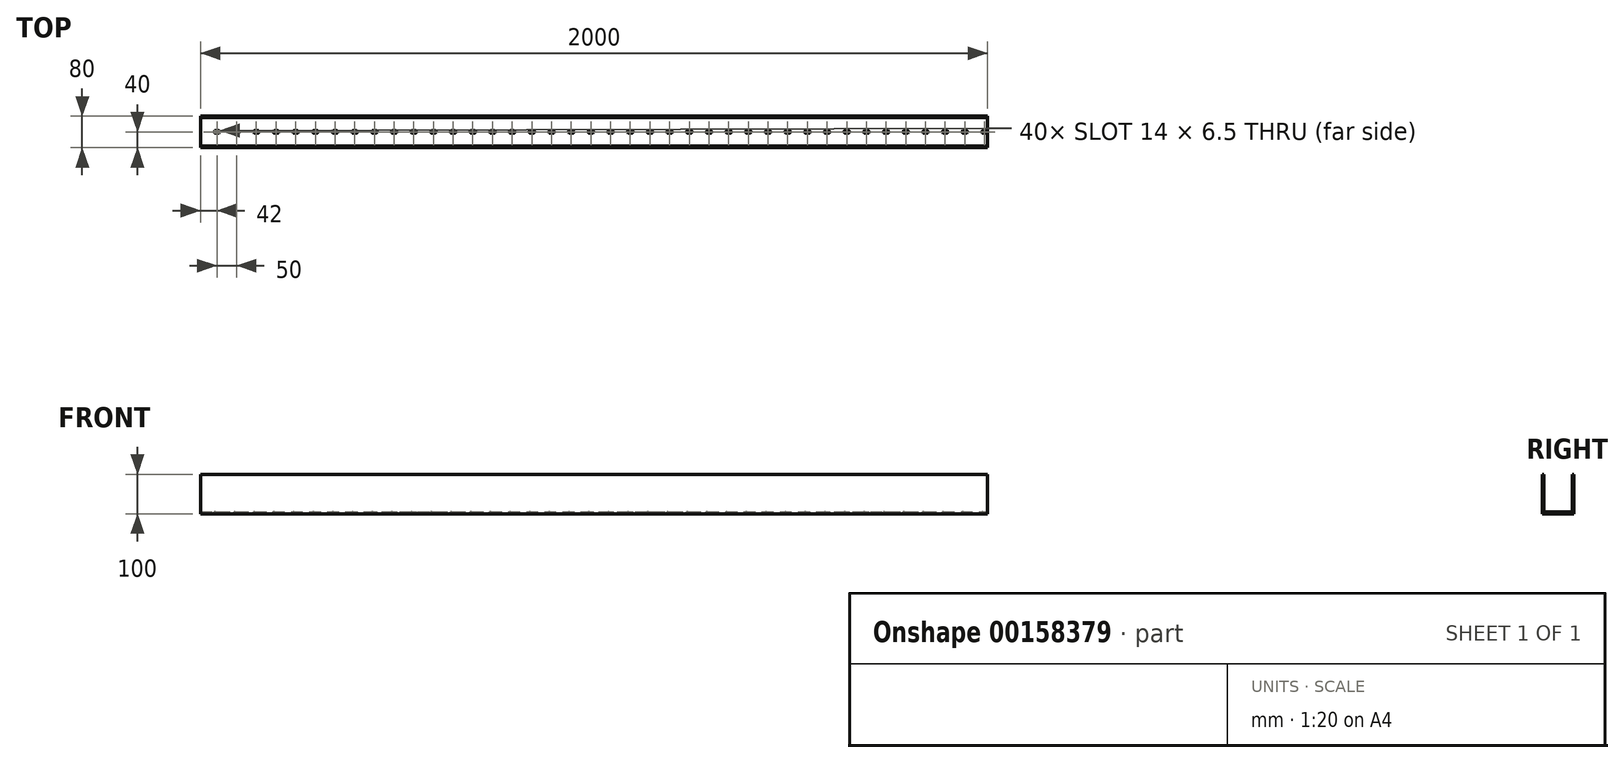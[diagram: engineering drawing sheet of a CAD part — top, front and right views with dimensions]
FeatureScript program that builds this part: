
annotation { "Feature Type Name" : "Feature", "Feature Type Description" : "" }
export const myFeature = defineFeature(function(context is Context, id is Id, definition is map)
    precondition{}
    {
        {
            var Q0;
            Q0=qCreatedBy(makeId("Top.planeOp"),FACE);
            var sketch = newSketch(context, id + "F0", { "sketchPlane" : qUnion([Q0])});
            skLineSegment(sketch, "E0.bottom", {"start": v(0, 0) * mm, "end": v(2000, 0) * mm});
            skLineSegment(sketch, "E0.top", {"start": v(0, 80) * mm, "end": v(2000, 80) * mm});
            skLineSegment(sketch, "E0.left", {"start": v(0, 0) * mm, "end": v(0, 80) * mm});
            skLineSegment(sketch, "E0.right", {"start": v(2000, 0) * mm, "end": v(2000, 80) * mm});
            skSolve(sketch);
        }
        {
            var Q0;
            Q0 = qSketchRegion(id + "F0", true);
            extrude(context, id + "F1", {"entities" : qUnion([Q0]), "depth" : 100 * mm});
        }
        {
            var Q0;
            Q0=makeQuery(id+"F1.opExtrude","CAP_FACE",FACE,{"disambiguationData":[OSD([sQuery(id+"F0.wireOp",EDGE,"E0.bottom"),sQuery(id+"F0.wireOp",EDGE,"E0.top"),sQuery(id+"F0.wireOp",EDGE,"E0.left"),sQuery(id+"F0.wireOp",EDGE,"E0.right")])],"isStart":false});
            var sketch = newSketch(context, id + "F2", { "sketchPlane" : qUnion([Q0])});
            skLineSegment(sketch, "E1.bottom", {"start": v(0, 76) * mm, "end": v(2000, 76) * mm});
            skLineSegment(sketch, "E1.top", {"start": v(0, 4) * mm, "end": v(2000, 4) * mm});
            skLineSegment(sketch, "E1.left", {"start": v(0, 76) * mm, "end": v(0, 4) * mm});
            skLineSegment(sketch, "E1.right", {"start": v(2000, 76) * mm, "end": v(2000, 4) * mm});
            skSolve(sketch);
        }
        {
            var Q0;
            Q0 = qSketchRegion(id + "F2", true);
            extrude(context, id + "F3", {"entities" : qUnion([Q0]), "operationType" : NewBodyOperationType.REMOVE, "oppositeDirection" : true, "depth" : (100 - 4) * mm});
        }
        {
            var Q0;
            Q0=makeQuery(id+"F3.boolean.opBoolean","COPY",FACE,{"derivedFrom":makeQuery(id+"F3.opExtrude","CAP_FACE",FACE,{"disambiguationData":[OSD([sQuery(id+"F2.wireOp",EDGE,"E1.bottom"),sQuery(id+"F2.wireOp",EDGE,"E1.top"),sQuery(id+"F2.wireOp",EDGE,"E1.left"),sQuery(id+"F2.wireOp",EDGE,"E1.right")])],"isStart":false})});
            var sketch = newSketch(context, id + "F4", { "sketchPlane" : qUnion([Q0])});
            skLineSegment(sketch, "E2", {"start": v(38.25, 40) * mm, "end": v(45.75, 40) * mm, "construction": true});
            skArc(sketch, "E3.0.startCap", {"start": v(38.25, 36.75) * mm, "mid": v(35, 40) * mm, "end": v(38.25, 43.25) * mm});
            skArc(sketch, "E3.0.endCap", {"start": v(45.75, 43.25) * mm, "mid": v(49, 40) * mm, "end": v(45.75, 36.75) * mm});
            skLineSegment(sketch, "E3.0.left", {"start": v(38.25, 43.25) * mm, "end": v(45.75, 43.25) * mm});
            skLineSegment(sketch, "E3.0.right", {"start": v(38.25, 36.75) * mm, "end": v(45.75, 36.75) * mm});
            skLineSegment(sketch, "E4.1.0.0", {"start": v(88.25, 36.75) * mm, "end": v(95.75, 36.75) * mm});
            skArc(sketch, "E4.1.0.1", {"start": v(88.25, 36.75) * mm, "mid": v(85, 40) * mm, "end": v(88.25, 43.25) * mm});
            skLineSegment(sketch, "E4.1.0.2", {"start": v(88.25, 43.25) * mm, "end": v(95.75, 43.25) * mm});
            skArc(sketch, "E4.1.0.3", {"start": v(95.75, 43.25) * mm, "mid": v(99, 40) * mm, "end": v(95.75, 36.75) * mm});
            skLineSegment(sketch, "E4.2.0.0", {"start": v(138.25, 36.75) * mm, "end": v(145.75, 36.75) * mm});
            skArc(sketch, "E4.2.0.1", {"start": v(138.25, 36.75) * mm, "mid": v(135, 40) * mm, "end": v(138.25, 43.25) * mm});
            skLineSegment(sketch, "E4.2.0.2", {"start": v(138.25, 43.25) * mm, "end": v(145.75, 43.25) * mm});
            skArc(sketch, "E4.2.0.3", {"start": v(145.75, 43.25) * mm, "mid": v(149, 40) * mm, "end": v(145.75, 36.75) * mm});
            skLineSegment(sketch, "E4.3.0.0", {"start": v(188.25, 36.75) * mm, "end": v(195.75, 36.75) * mm});
            skArc(sketch, "E4.3.0.1", {"start": v(188.25, 36.75) * mm, "mid": v(185, 40) * mm, "end": v(188.25, 43.25) * mm});
            skLineSegment(sketch, "E4.3.0.2", {"start": v(188.25, 43.25) * mm, "end": v(195.75, 43.25) * mm});
            skArc(sketch, "E4.3.0.3", {"start": v(195.75, 43.25) * mm, "mid": v(199, 40) * mm, "end": v(195.75, 36.75) * mm});
            skLineSegment(sketch, "E4.4.0.0", {"start": v(238.25, 36.75) * mm, "end": v(245.75, 36.75) * mm});
            skArc(sketch, "E4.4.0.1", {"start": v(238.25, 36.75) * mm, "mid": v(235, 40) * mm, "end": v(238.25, 43.25) * mm});
            skLineSegment(sketch, "E4.4.0.2", {"start": v(238.25, 43.25) * mm, "end": v(245.75, 43.25) * mm});
            skArc(sketch, "E4.4.0.3", {"start": v(245.75, 43.25) * mm, "mid": v(249, 40) * mm, "end": v(245.75, 36.75) * mm});
            skLineSegment(sketch, "E4.5.0.0", {"start": v(288.25, 36.75) * mm, "end": v(295.75, 36.75) * mm});
            skArc(sketch, "E4.5.0.1", {"start": v(288.25, 36.75) * mm, "mid": v(285, 40) * mm, "end": v(288.25, 43.25) * mm});
            skLineSegment(sketch, "E4.5.0.2", {"start": v(288.25, 43.25) * mm, "end": v(295.75, 43.25) * mm});
            skArc(sketch, "E4.5.0.3", {"start": v(295.75, 43.25) * mm, "mid": v(299, 40) * mm, "end": v(295.75, 36.75) * mm});
            skLineSegment(sketch, "E4.6.0.0", {"start": v(338.25, 36.75) * mm, "end": v(345.75, 36.75) * mm});
            skArc(sketch, "E4.6.0.1", {"start": v(338.25, 36.75) * mm, "mid": v(335, 40) * mm, "end": v(338.25, 43.25) * mm});
            skLineSegment(sketch, "E4.6.0.2", {"start": v(338.25, 43.25) * mm, "end": v(345.75, 43.25) * mm});
            skArc(sketch, "E4.6.0.3", {"start": v(345.75, 43.25) * mm, "mid": v(349, 40) * mm, "end": v(345.75, 36.75) * mm});
            skLineSegment(sketch, "E4.7.0.0", {"start": v(388.25, 36.75) * mm, "end": v(395.75, 36.75) * mm});
            skArc(sketch, "E4.7.0.1", {"start": v(388.25, 36.75) * mm, "mid": v(385, 40) * mm, "end": v(388.25, 43.25) * mm});
            skLineSegment(sketch, "E4.7.0.2", {"start": v(388.25, 43.25) * mm, "end": v(395.75, 43.25) * mm});
            skArc(sketch, "E4.7.0.3", {"start": v(395.75, 43.25) * mm, "mid": v(399, 40) * mm, "end": v(395.75, 36.75) * mm});
            skLineSegment(sketch, "E4.8.0.0", {"start": v(438.25, 36.75) * mm, "end": v(445.75, 36.75) * mm});
            skArc(sketch, "E4.8.0.1", {"start": v(438.25, 36.75) * mm, "mid": v(435, 40) * mm, "end": v(438.25, 43.25) * mm});
            skLineSegment(sketch, "E4.8.0.2", {"start": v(438.25, 43.25) * mm, "end": v(445.75, 43.25) * mm});
            skArc(sketch, "E4.8.0.3", {"start": v(445.75, 43.25) * mm, "mid": v(449, 40) * mm, "end": v(445.75, 36.75) * mm});
            skLineSegment(sketch, "E4.9.0.0", {"start": v(488.25, 36.75) * mm, "end": v(495.75, 36.75) * mm});
            skArc(sketch, "E4.9.0.1", {"start": v(488.25, 36.75) * mm, "mid": v(485, 40) * mm, "end": v(488.25, 43.25) * mm});
            skLineSegment(sketch, "E4.9.0.2", {"start": v(488.25, 43.25) * mm, "end": v(495.75, 43.25) * mm});
            skArc(sketch, "E4.9.0.3", {"start": v(495.75, 43.25) * mm, "mid": v(499, 40) * mm, "end": v(495.75, 36.75) * mm});
            skLineSegment(sketch, "E4.10.0.0", {"start": v(538.25, 36.75) * mm, "end": v(545.75, 36.75) * mm});
            skArc(sketch, "E4.10.0.1", {"start": v(538.25, 36.75) * mm, "mid": v(535, 40) * mm, "end": v(538.25, 43.25) * mm});
            skLineSegment(sketch, "E4.10.0.2", {"start": v(538.25, 43.25) * mm, "end": v(545.75, 43.25) * mm});
            skArc(sketch, "E4.10.0.3", {"start": v(545.75, 43.25) * mm, "mid": v(549, 40) * mm, "end": v(545.75, 36.75) * mm});
            skLineSegment(sketch, "E4.11.0.0", {"start": v(588.25, 36.75) * mm, "end": v(595.75, 36.75) * mm});
            skArc(sketch, "E4.11.0.1", {"start": v(588.25, 36.75) * mm, "mid": v(585, 40) * mm, "end": v(588.25, 43.25) * mm});
            skLineSegment(sketch, "E4.11.0.2", {"start": v(588.25, 43.25) * mm, "end": v(595.75, 43.25) * mm});
            skArc(sketch, "E4.11.0.3", {"start": v(595.75, 43.25) * mm, "mid": v(599, 40) * mm, "end": v(595.75, 36.75) * mm});
            skLineSegment(sketch, "E4.12.0.0", {"start": v(638.25, 36.75) * mm, "end": v(645.75, 36.75) * mm});
            skArc(sketch, "E4.12.0.1", {"start": v(638.25, 36.75) * mm, "mid": v(635, 40) * mm, "end": v(638.25, 43.25) * mm});
            skLineSegment(sketch, "E4.12.0.2", {"start": v(638.25, 43.25) * mm, "end": v(645.75, 43.25) * mm});
            skArc(sketch, "E4.12.0.3", {"start": v(645.75, 43.25) * mm, "mid": v(649, 40) * mm, "end": v(645.75, 36.75) * mm});
            skLineSegment(sketch, "E4.13.0.0", {"start": v(688.25, 36.75) * mm, "end": v(695.75, 36.75) * mm});
            skArc(sketch, "E4.13.0.1", {"start": v(688.25, 36.75) * mm, "mid": v(685, 40) * mm, "end": v(688.25, 43.25) * mm});
            skLineSegment(sketch, "E4.13.0.2", {"start": v(688.25, 43.25) * mm, "end": v(695.75, 43.25) * mm});
            skArc(sketch, "E4.13.0.3", {"start": v(695.75, 43.25) * mm, "mid": v(699, 40) * mm, "end": v(695.75, 36.75) * mm});
            skLineSegment(sketch, "E4.14.0.0", {"start": v(738.25, 36.75) * mm, "end": v(745.75, 36.75) * mm});
            skArc(sketch, "E4.14.0.1", {"start": v(738.25, 36.75) * mm, "mid": v(735, 40) * mm, "end": v(738.25, 43.25) * mm});
            skLineSegment(sketch, "E4.14.0.2", {"start": v(738.25, 43.25) * mm, "end": v(745.75, 43.25) * mm});
            skArc(sketch, "E4.14.0.3", {"start": v(745.75, 43.25) * mm, "mid": v(749, 40) * mm, "end": v(745.75, 36.75) * mm});
            skLineSegment(sketch, "E4.15.0.0", {"start": v(788.25, 36.75) * mm, "end": v(795.75, 36.75) * mm});
            skArc(sketch, "E4.15.0.1", {"start": v(788.25, 36.75) * mm, "mid": v(785, 40) * mm, "end": v(788.25, 43.25) * mm});
            skLineSegment(sketch, "E4.15.0.2", {"start": v(788.25, 43.25) * mm, "end": v(795.75, 43.25) * mm});
            skArc(sketch, "E4.15.0.3", {"start": v(795.75, 43.25) * mm, "mid": v(799, 40) * mm, "end": v(795.75, 36.75) * mm});
            skLineSegment(sketch, "E4.16.0.0", {"start": v(838.25, 36.75) * mm, "end": v(845.75, 36.75) * mm});
            skArc(sketch, "E4.16.0.1", {"start": v(838.25, 36.75) * mm, "mid": v(835, 40) * mm, "end": v(838.25, 43.25) * mm});
            skLineSegment(sketch, "E4.16.0.2", {"start": v(838.25, 43.25) * mm, "end": v(845.75, 43.25) * mm});
            skArc(sketch, "E4.16.0.3", {"start": v(845.75, 43.25) * mm, "mid": v(849, 40) * mm, "end": v(845.75, 36.75) * mm});
            skLineSegment(sketch, "E4.17.0.0", {"start": v(888.25, 36.75) * mm, "end": v(895.75, 36.75) * mm});
            skArc(sketch, "E4.17.0.1", {"start": v(888.25, 36.75) * mm, "mid": v(885, 40) * mm, "end": v(888.25, 43.25) * mm});
            skLineSegment(sketch, "E4.17.0.2", {"start": v(888.25, 43.25) * mm, "end": v(895.75, 43.25) * mm});
            skArc(sketch, "E4.17.0.3", {"start": v(895.75, 43.25) * mm, "mid": v(899, 40) * mm, "end": v(895.75, 36.75) * mm});
            skLineSegment(sketch, "E4.18.0.0", {"start": v(938.25, 36.75) * mm, "end": v(945.75, 36.75) * mm});
            skArc(sketch, "E4.18.0.1", {"start": v(938.25, 36.75) * mm, "mid": v(935, 40) * mm, "end": v(938.25, 43.25) * mm});
            skLineSegment(sketch, "E4.18.0.2", {"start": v(938.25, 43.25) * mm, "end": v(945.75, 43.25) * mm});
            skArc(sketch, "E4.18.0.3", {"start": v(945.75, 43.25) * mm, "mid": v(949, 40) * mm, "end": v(945.75, 36.75) * mm});
            skLineSegment(sketch, "E4.19.0.0", {"start": v(988.25, 36.75) * mm, "end": v(995.75, 36.75) * mm});
            skArc(sketch, "E4.19.0.1", {"start": v(988.25, 36.75) * mm, "mid": v(985, 40) * mm, "end": v(988.25, 43.25) * mm});
            skLineSegment(sketch, "E4.19.0.2", {"start": v(988.25, 43.25) * mm, "end": v(995.75, 43.25) * mm});
            skArc(sketch, "E4.19.0.3", {"start": v(995.75, 43.25) * mm, "mid": v(999, 40) * mm, "end": v(995.75, 36.75) * mm});
            skLineSegment(sketch, "E4.20.0.0", {"start": v(1038.25, 36.75) * mm, "end": v(1045.75, 36.75) * mm});
            skArc(sketch, "E4.20.0.1", {"start": v(1038.25, 36.75) * mm, "mid": v(1035, 40) * mm, "end": v(1038.25, 43.25) * mm});
            skLineSegment(sketch, "E4.20.0.2", {"start": v(1038.25, 43.25) * mm, "end": v(1045.75, 43.25) * mm});
            skArc(sketch, "E4.20.0.3", {"start": v(1045.75, 43.25) * mm, "mid": v(1049, 40) * mm, "end": v(1045.75, 36.75) * mm});
            skLineSegment(sketch, "E4.21.0.0", {"start": v(1088.25, 36.75) * mm, "end": v(1095.75, 36.75) * mm});
            skArc(sketch, "E4.21.0.1", {"start": v(1088.25, 36.75) * mm, "mid": v(1085, 40) * mm, "end": v(1088.25, 43.25) * mm});
            skLineSegment(sketch, "E4.21.0.2", {"start": v(1088.25, 43.25) * mm, "end": v(1095.75, 43.25) * mm});
            skArc(sketch, "E4.21.0.3", {"start": v(1095.75, 43.25) * mm, "mid": v(1099, 40) * mm, "end": v(1095.75, 36.75) * mm});
            skLineSegment(sketch, "E4.22.0.0", {"start": v(1138.25, 36.75) * mm, "end": v(1145.75, 36.75) * mm});
            skArc(sketch, "E4.22.0.1", {"start": v(1138.25, 36.75) * mm, "mid": v(1135, 40) * mm, "end": v(1138.25, 43.25) * mm});
            skLineSegment(sketch, "E4.22.0.2", {"start": v(1138.25, 43.25) * mm, "end": v(1145.75, 43.25) * mm});
            skArc(sketch, "E4.22.0.3", {"start": v(1145.75, 43.25) * mm, "mid": v(1149, 40) * mm, "end": v(1145.75, 36.75) * mm});
            skLineSegment(sketch, "E4.23.0.0", {"start": v(1188.25, 36.75) * mm, "end": v(1195.75, 36.75) * mm});
            skArc(sketch, "E4.23.0.1", {"start": v(1188.25, 36.75) * mm, "mid": v(1185, 40) * mm, "end": v(1188.25, 43.25) * mm});
            skLineSegment(sketch, "E4.23.0.2", {"start": v(1188.25, 43.25) * mm, "end": v(1195.75, 43.25) * mm});
            skArc(sketch, "E4.23.0.3", {"start": v(1195.75, 43.25) * mm, "mid": v(1199, 40) * mm, "end": v(1195.75, 36.75) * mm});
            skLineSegment(sketch, "E4.24.0.0", {"start": v(1238.25, 36.75) * mm, "end": v(1245.75, 36.75) * mm});
            skArc(sketch, "E4.24.0.1", {"start": v(1238.25, 36.75) * mm, "mid": v(1235, 40) * mm, "end": v(1238.25, 43.25) * mm});
            skLineSegment(sketch, "E4.24.0.2", {"start": v(1238.25, 43.25) * mm, "end": v(1245.75, 43.25) * mm});
            skArc(sketch, "E4.24.0.3", {"start": v(1245.75, 43.25) * mm, "mid": v(1249, 40) * mm, "end": v(1245.75, 36.75) * mm});
            skLineSegment(sketch, "E4.25.0.0", {"start": v(1288.25, 36.75) * mm, "end": v(1295.75, 36.75) * mm});
            skArc(sketch, "E4.25.0.1", {"start": v(1288.25, 36.75) * mm, "mid": v(1285, 40) * mm, "end": v(1288.25, 43.25) * mm});
            skLineSegment(sketch, "E4.25.0.2", {"start": v(1288.25, 43.25) * mm, "end": v(1295.75, 43.25) * mm});
            skArc(sketch, "E4.25.0.3", {"start": v(1295.75, 43.25) * mm, "mid": v(1299, 40) * mm, "end": v(1295.75, 36.75) * mm});
            skLineSegment(sketch, "E4.26.0.0", {"start": v(1338.25, 36.75) * mm, "end": v(1345.75, 36.75) * mm});
            skArc(sketch, "E4.26.0.1", {"start": v(1338.25, 36.75) * mm, "mid": v(1335, 40) * mm, "end": v(1338.25, 43.25) * mm});
            skLineSegment(sketch, "E4.26.0.2", {"start": v(1338.25, 43.25) * mm, "end": v(1345.75, 43.25) * mm});
            skArc(sketch, "E4.26.0.3", {"start": v(1345.75, 43.25) * mm, "mid": v(1349, 40) * mm, "end": v(1345.75, 36.75) * mm});
            skLineSegment(sketch, "E4.27.0.0", {"start": v(1388.25, 36.75) * mm, "end": v(1395.75, 36.75) * mm});
            skArc(sketch, "E4.27.0.1", {"start": v(1388.25, 36.75) * mm, "mid": v(1385, 40) * mm, "end": v(1388.25, 43.25) * mm});
            skLineSegment(sketch, "E4.27.0.2", {"start": v(1388.25, 43.25) * mm, "end": v(1395.75, 43.25) * mm});
            skArc(sketch, "E4.27.0.3", {"start": v(1395.75, 43.25) * mm, "mid": v(1399, 40) * mm, "end": v(1395.75, 36.75) * mm});
            skLineSegment(sketch, "E4.28.0.0", {"start": v(1438.25, 36.75) * mm, "end": v(1445.75, 36.75) * mm});
            skArc(sketch, "E4.28.0.1", {"start": v(1438.25, 36.75) * mm, "mid": v(1435, 40) * mm, "end": v(1438.25, 43.25) * mm});
            skLineSegment(sketch, "E4.28.0.2", {"start": v(1438.25, 43.25) * mm, "end": v(1445.75, 43.25) * mm});
            skArc(sketch, "E4.28.0.3", {"start": v(1445.75, 43.25) * mm, "mid": v(1449, 40) * mm, "end": v(1445.75, 36.75) * mm});
            skLineSegment(sketch, "E4.29.0.0", {"start": v(1488.25, 36.75) * mm, "end": v(1495.75, 36.75) * mm});
            skArc(sketch, "E4.29.0.1", {"start": v(1488.25, 36.75) * mm, "mid": v(1485, 40) * mm, "end": v(1488.25, 43.25) * mm});
            skLineSegment(sketch, "E4.29.0.2", {"start": v(1488.25, 43.25) * mm, "end": v(1495.75, 43.25) * mm});
            skArc(sketch, "E4.29.0.3", {"start": v(1495.75, 43.25) * mm, "mid": v(1499, 40) * mm, "end": v(1495.75, 36.75) * mm});
            skLineSegment(sketch, "E4.30.0.0", {"start": v(1538.25, 36.75) * mm, "end": v(1545.75, 36.75) * mm});
            skArc(sketch, "E4.30.0.1", {"start": v(1538.25, 36.75) * mm, "mid": v(1535, 40) * mm, "end": v(1538.25, 43.25) * mm});
            skLineSegment(sketch, "E4.30.0.2", {"start": v(1538.25, 43.25) * mm, "end": v(1545.75, 43.25) * mm});
            skArc(sketch, "E4.30.0.3", {"start": v(1545.75, 43.25) * mm, "mid": v(1549, 40) * mm, "end": v(1545.75, 36.75) * mm});
            skLineSegment(sketch, "E4.31.0.0", {"start": v(1588.25, 36.75) * mm, "end": v(1595.75, 36.75) * mm});
            skArc(sketch, "E4.31.0.1", {"start": v(1588.25, 36.75) * mm, "mid": v(1585, 40) * mm, "end": v(1588.25, 43.25) * mm});
            skLineSegment(sketch, "E4.31.0.2", {"start": v(1588.25, 43.25) * mm, "end": v(1595.75, 43.25) * mm});
            skArc(sketch, "E4.31.0.3", {"start": v(1595.75, 43.25) * mm, "mid": v(1599, 40) * mm, "end": v(1595.75, 36.75) * mm});
            skLineSegment(sketch, "E4.32.0.0", {"start": v(1638.25, 36.75) * mm, "end": v(1645.75, 36.75) * mm});
            skArc(sketch, "E4.32.0.1", {"start": v(1638.25, 36.75) * mm, "mid": v(1635, 40) * mm, "end": v(1638.25, 43.25) * mm});
            skLineSegment(sketch, "E4.32.0.2", {"start": v(1638.25, 43.25) * mm, "end": v(1645.75, 43.25) * mm});
            skArc(sketch, "E4.32.0.3", {"start": v(1645.75, 43.25) * mm, "mid": v(1649, 40) * mm, "end": v(1645.75, 36.75) * mm});
            skLineSegment(sketch, "E4.33.0.0", {"start": v(1688.25, 36.75) * mm, "end": v(1695.75, 36.75) * mm});
            skArc(sketch, "E4.33.0.1", {"start": v(1688.25, 36.75) * mm, "mid": v(1685, 40) * mm, "end": v(1688.25, 43.25) * mm});
            skLineSegment(sketch, "E4.33.0.2", {"start": v(1688.25, 43.25) * mm, "end": v(1695.75, 43.25) * mm});
            skArc(sketch, "E4.33.0.3", {"start": v(1695.75, 43.25) * mm, "mid": v(1699, 40) * mm, "end": v(1695.75, 36.75) * mm});
            skLineSegment(sketch, "E4.34.0.0", {"start": v(1738.25, 36.75) * mm, "end": v(1745.75, 36.75) * mm});
            skArc(sketch, "E4.34.0.1", {"start": v(1738.25, 36.75) * mm, "mid": v(1735, 40) * mm, "end": v(1738.25, 43.25) * mm});
            skLineSegment(sketch, "E4.34.0.2", {"start": v(1738.25, 43.25) * mm, "end": v(1745.75, 43.25) * mm});
            skArc(sketch, "E4.34.0.3", {"start": v(1745.75, 43.25) * mm, "mid": v(1749, 40) * mm, "end": v(1745.75, 36.75) * mm});
            skLineSegment(sketch, "E4.35.0.0", {"start": v(1788.25, 36.75) * mm, "end": v(1795.75, 36.75) * mm});
            skArc(sketch, "E4.35.0.1", {"start": v(1788.25, 36.75) * mm, "mid": v(1785, 40) * mm, "end": v(1788.25, 43.25) * mm});
            skLineSegment(sketch, "E4.35.0.2", {"start": v(1788.25, 43.25) * mm, "end": v(1795.75, 43.25) * mm});
            skArc(sketch, "E4.35.0.3", {"start": v(1795.75, 43.25) * mm, "mid": v(1799, 40) * mm, "end": v(1795.75, 36.75) * mm});
            skLineSegment(sketch, "E4.36.0.0", {"start": v(1838.25, 36.75) * mm, "end": v(1845.75, 36.75) * mm});
            skArc(sketch, "E4.36.0.1", {"start": v(1838.25, 36.75) * mm, "mid": v(1835, 40) * mm, "end": v(1838.25, 43.25) * mm});
            skLineSegment(sketch, "E4.36.0.2", {"start": v(1838.25, 43.25) * mm, "end": v(1845.75, 43.25) * mm});
            skArc(sketch, "E4.36.0.3", {"start": v(1845.75, 43.25) * mm, "mid": v(1849, 40) * mm, "end": v(1845.75, 36.75) * mm});
            skLineSegment(sketch, "E4.37.0.0", {"start": v(1888.25, 36.75) * mm, "end": v(1895.75, 36.75) * mm});
            skArc(sketch, "E4.37.0.1", {"start": v(1888.25, 36.75) * mm, "mid": v(1885, 40) * mm, "end": v(1888.25, 43.25) * mm});
            skLineSegment(sketch, "E4.37.0.2", {"start": v(1888.25, 43.25) * mm, "end": v(1895.75, 43.25) * mm});
            skArc(sketch, "E4.37.0.3", {"start": v(1895.75, 43.25) * mm, "mid": v(1899, 40) * mm, "end": v(1895.75, 36.75) * mm});
            skLineSegment(sketch, "E4.38.0.0", {"start": v(1938.25, 36.75) * mm, "end": v(1945.75, 36.75) * mm});
            skArc(sketch, "E4.38.0.1", {"start": v(1938.25, 36.75) * mm, "mid": v(1935, 40) * mm, "end": v(1938.25, 43.25) * mm});
            skLineSegment(sketch, "E4.38.0.2", {"start": v(1938.25, 43.25) * mm, "end": v(1945.75, 43.25) * mm});
            skArc(sketch, "E4.38.0.3", {"start": v(1945.75, 43.25) * mm, "mid": v(1949, 40) * mm, "end": v(1945.75, 36.75) * mm});
            skLineSegment(sketch, "E4.39.0.0", {"start": v(1988.25, 36.75) * mm, "end": v(1995.75, 36.75) * mm});
            skArc(sketch, "E4.39.0.1", {"start": v(1988.25, 36.75) * mm, "mid": v(1985, 40) * mm, "end": v(1988.25, 43.25) * mm});
            skLineSegment(sketch, "E4.39.0.2", {"start": v(1988.25, 43.25) * mm, "end": v(1995.75, 43.25) * mm});
            skArc(sketch, "E4.39.0.3", {"start": v(1995.75, 43.25) * mm, "mid": v(1999, 40) * mm, "end": v(1995.75, 36.75) * mm});
            skLineSegment(sketch, "E4.direction1", {"start": v(38.25, 36.75) * mm, "end": v(88.25, 36.75) * mm, "construction": true});
            skSolve(sketch);
        }
        {
            var Q0;
            Q0 = qSketchRegion(id + "F4", true);
            extrude(context, id + "F5", {"entities" : qUnion([Q0]), "operationType" : NewBodyOperationType.REMOVE, "endBound" : BoundingType.THROUGH_ALL, "oppositeDirection" : true, "depth" : 25 * mm});
        }
    });
